# Revit family: Paper_Towel_Dispenser_Bobrick_B-39617
name_source: partatom
category: Generic Models
revit_build: Autodesk Revit 2016 (Build: 20150714_1515(x64)
units: mm (PartAtom-declared; Revit-internal decimal feet)

## family parameters
Can host rebar = No
Cut with Voids When Loaded = Yes
Host = Face
OmniClass Number = 23.40.20.21.34
OmniClass Title = Soap Holders, Dispensers
Part Type = Normal
Room Calculation Point = No
Round Connector Dimension = Use Diameter
Shared = Yes

## types (1)
- B-39617
    Assembly Code = E2020200
    Default Elevation = 40"
    Description = B-39617 ClassicSeries Recessed Convertible Paper Towel Dispenser/Waste Receptacle
    Height = 56"
    Installation Type = Surface Mounted
    Length = 17 3/16"
    Manufacturer = Bobrick
    Material = Metal_Bobrick_Stainless-Steel
    Model = B-39617
    Product Documentation Link = https://www.bobrick.com
    Product Page URL = https://www.bobrick.com
    URL = http://www.bobrick.com
    Warranty Documentation Link = https://www.bobrick.com
    Width = 9 1/16"

## geometry (parser evidence)
native form markers: Sweep x2
no freeform markers — native parametric forms only
